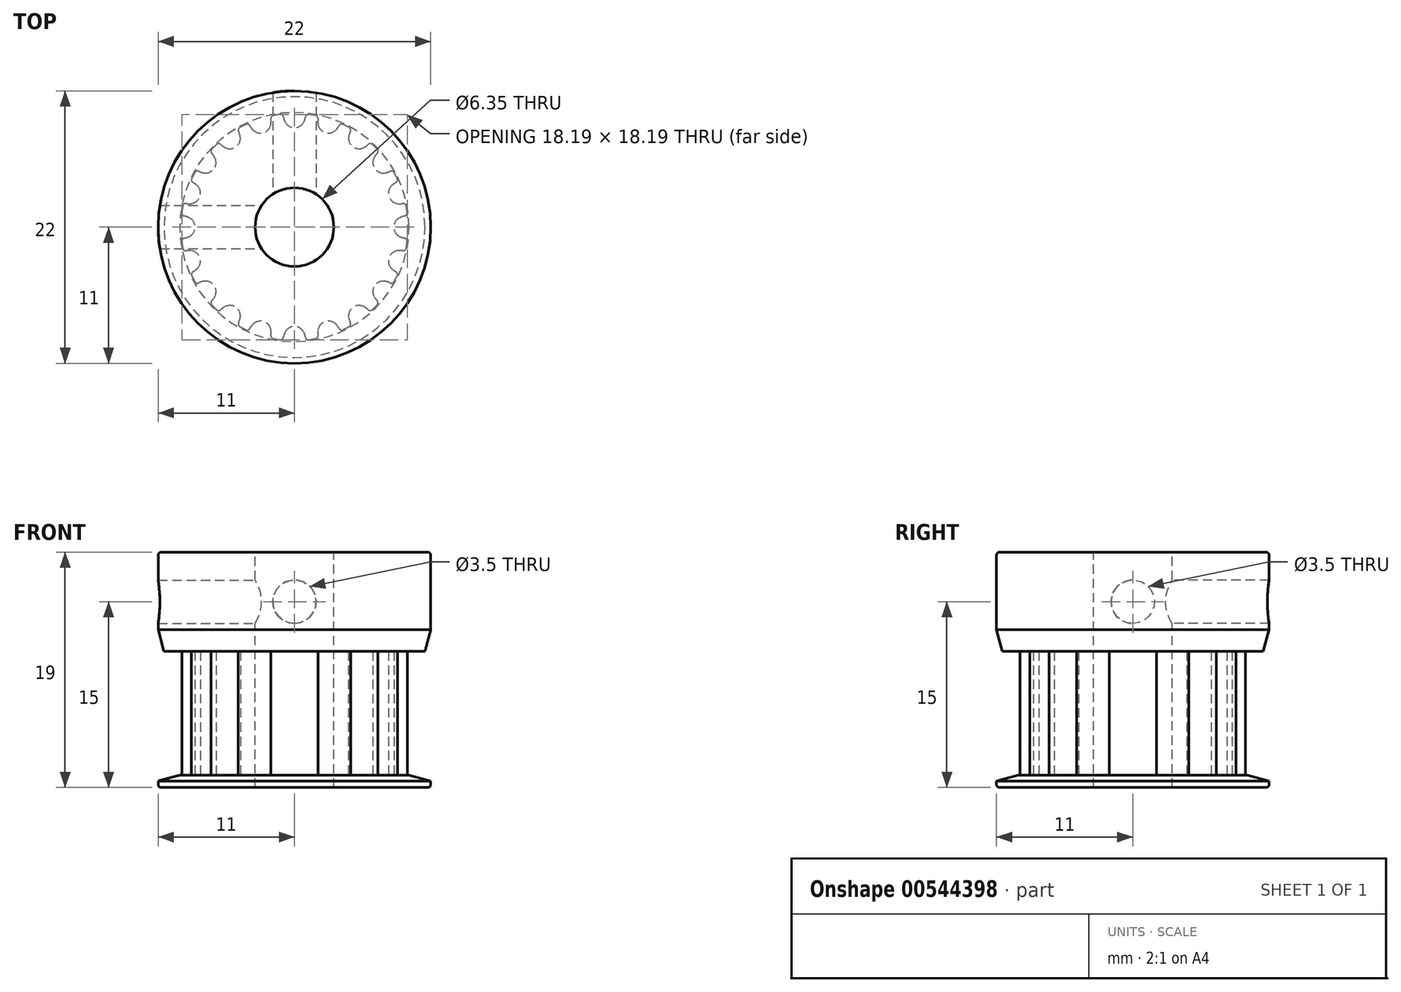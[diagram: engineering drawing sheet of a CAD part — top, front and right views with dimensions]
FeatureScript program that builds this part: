
annotation { "Feature Type Name" : "Feature", "Feature Type Description" : "" }
export const myFeature = defineFeature(function(context is Context, id is Id, definition is map)
    precondition{}
    {
        {
            assignVariable(context, id + "F0", {"name" : "teeth", "anyValue" : 20});
        }
        {
            assignVariable(context, id + "F1", {"name" : "width", "anyValue" : 10});
        }
        {
            var Q0;
            Q0=qCreatedBy(makeId("Top.planeOp"),FACE);
            var sketch = newSketch(context, id + "F2", { "sketchPlane" : qUnion([Q0])});
            skLineSegment(sketch, "E0", {"start": v(0, 0) * mm, "end": v(0, 8.02) * mm, "construction": true});
            skArc(sketch, "E1", {"start": v(2.35, 8.86) * mm, "mid": v(0, 9.17) * mm, "end": v(-2.35, 8.86) * mm, "construction": true});
            skArc(sketch, "E2", {"start": v(0, 8.02) * mm, "mid": v(0.46, 8.15) * mm, "end": v(0.77, 8.52) * mm});
            skLineSegment(sketch, "E3", {"start": v(0, 8.02) * mm, "end": v(0, 9.17) * mm, "construction": true});
            skLineSegment(sketch, "E4", {"start": v(0, 9.17) * mm, "end": v(0, 9.55) * mm, "construction": true});
            skArc(sketch, "E5", {"start": v(1.5, 9.43) * mm, "mid": v(0, 9.55) * mm, "end": v(-1.5, 9.43) * mm, "construction": true});
            skLineSegment(sketch, "E6", {"start": v(1.43, 9.06) * mm, "end": v(0, 0) * mm});
            skLineSegment(sketch, "E7", {"start": v(0, 0) * mm, "end": v(-1.43, 9.06) * mm});
            skArc(sketch, "E8", {"start": v(1.17, 9.1) * mm, "mid": v(0.99, 9.05) * mm, "end": v(0.89, 8.89) * mm});
            skArc(sketch, "E9", {"start": v(0.77, 8.52) * mm, "mid": v(0.84, 8.7) * mm, "end": v(0.89, 8.89) * mm});
            skArc(sketch, "E10.MirrorCS", {"start": v(0, 8.02) * mm, "mid": v(-0.46, 8.15) * mm, "end": v(-0.77, 8.52) * mm});
            skArc(sketch, "E11.MirrorCS", {"start": v(-0.77, 8.52) * mm, "mid": v(-0.84, 8.7) * mm, "end": v(-0.89, 8.89) * mm});
            skArc(sketch, "E12.MirrorCS", {"start": v(-1.17, 9.1) * mm, "mid": v(-0.99, 9.05) * mm, "end": v(-0.89, 8.89) * mm});
            skArc(sketch, "E13", {"start": v(0, 9.17) * mm, "mid": v(-0.3, 9.16) * mm, "end": v(-0.6, 9.15) * mm, "construction": true});
            skArc(sketch, "E14", {"start": v(2.16, 7.72) * mm, "mid": v(0, 8.02) * mm, "end": v(-2.16, 7.72) * mm, "construction": true});
            skArc(sketch, "E15", {"start": v(-1.17, 9.1) * mm, "mid": v(-1.3, 9.08) * mm, "end": v(-1.43, 9.06) * mm});
            skArc(sketch, "E16", {"start": v(1.17, 9.1) * mm, "mid": v(1.3, 9.08) * mm, "end": v(1.43, 9.06) * mm});
            skPoint(sketch, "E17", {"position": v(0, 8.02) * mm});
            skSolve(sketch);
        }
        {
            var Q0;
            Q0=makeQuery(id+"F2.imprint","IMPRINT",FACE,{"disambiguationData":[TD([[makeQuery(id+"F2.imprint","IMPRINT",EDGE,{"derivedFrom":sQuery(id+"F2.wireOp",EDGE,"E2")}),-1.0]])]});
            var Q1;
            {var subQ1=sQuery(id+"F2.wireOp",EDGE,"N9a9pOVT-NxnP-9PMo-Yz0L-ytRW1WlfzG62");Q1=makeQuery(id+"F2.imprint","IMPRINT",FACE,{"disambiguationData":[TD([[makeQuery(id+"F2.imprint","IMPRINT",EDGE,{"derivedFrom":subQ1}),-1.0]])]});}
            var Q2;
            {var subQ0=sQuery(id+"F2.wireOp",EDGE,"E6");Q2=makeQuery(id+"F2.imprint","IMPRINT",FACE,{"disambiguationData":[TD([[makeQuery(id+"F2.imprint","IMPRINT",EDGE,{"derivedFrom":subQ0}),-1.0]])]});}
            extrude(context, id + "F3", {"entities" : qUnion([Q0, Q1, Q2]), "depth" : (getVariable(context, 'width')) * mm, "offsetDistance" : 25 * mm, "symmetric" : true});
        }
        {
            var Q0;
            Q0=makeQuery(id+"F3.opExtrude","SWEPT_BODY",BODY,{"disambiguationData":[OSD([sQuery(id+"F2.wireOp",EDGE,"E1"),sQuery(id+"F2.wireOp",EDGE,"E2"),sQuery(id+"F2.wireOp",EDGE,"WtW3y5By-gfdo-wMA2-XeKf-OYMCoWhlFWBV"),sQuery(id+"F2.wireOp",EDGE,"E6"),sQuery(id+"F2.wireOp",EDGE,"E7"),sQuery(id+"F2.wireOp",EDGE,"N9a9pOVT-NxnP-9PMo-Yz0L-ytRW1WlfzG62"),sQuery(id+"F2.wireOp",EDGE,"E8"),sQuery(id+"F2.wireOp",EDGE,"E9"),sQuery(id+"F2.wireOp",EDGE,"E10.MirrorCS"),sQuery(id+"F2.wireOp",EDGE,"E11.MirrorCS"),sQuery(id+"F2.wireOp",EDGE,"E12.MirrorCS")])]});
            var Q1;
            Q1=makeQuery(id+"F3.opExtrude","SWEPT_EDGE",EDGE,{"disambiguationData":[OSD([sQuery(id+"F2.wireOp",EDGE,"E6"),sQuery(id+"F2.wireOp",EDGE,"E7")])]});
            circularPattern(context, id + "F4", {"operationType" : NewBodyOperationType.ADD, "entities" : qUnion([Q0]), "axis" : qUnion([Q1]), "angle" : 360 * degree, "instanceCount" : getVariable(context, 'teeth'), "equalSpace" : true});
        }
        {
            var Q0;
            {var subQ0=makeQuery(id+"F3.opExtrude","CAP_FACE",FACE,{"disambiguationData":[OSD([sQuery(id+"F2.wireOp",EDGE,"E2"),sQuery(id+"F2.wireOp",EDGE,"E6"),sQuery(id+"F2.wireOp",EDGE,"E7"),sQuery(id+"F2.wireOp",EDGE,"E8"),sQuery(id+"F2.wireOp",EDGE,"E9"),sQuery(id+"F2.wireOp",EDGE,"E10.MirrorCS"),sQuery(id+"F2.wireOp",EDGE,"E11.MirrorCS"),sQuery(id+"F2.wireOp",EDGE,"E12.MirrorCS"),sQuery(id+"F2.wireOp",EDGE,"E15"),sQuery(id+"F2.wireOp",EDGE,"E16")])],"isStart":true});Q0=makeQuery(id+"F4.boolean.opBoolean","MERGE",FACE,{"derivedFrom":[subQ0,makeQuery(id+"F4.opPattern","COPY",FACE,{"derivedFrom":subQ0,"instanceName":"1"}),makeQuery(id+"F4.opPattern","COPY",FACE,{"derivedFrom":subQ0,"instanceName":"2"}),makeQuery(id+"F4.opPattern","COPY",FACE,{"derivedFrom":subQ0,"instanceName":"3"}),makeQuery(id+"F4.opPattern","COPY",FACE,{"derivedFrom":subQ0,"instanceName":"4"}),makeQuery(id+"F4.opPattern","COPY",FACE,{"derivedFrom":subQ0,"instanceName":"5"}),makeQuery(id+"F4.opPattern","COPY",FACE,{"derivedFrom":subQ0,"instanceName":"6"}),makeQuery(id+"F4.opPattern","COPY",FACE,{"derivedFrom":subQ0,"instanceName":"7"}),makeQuery(id+"F4.opPattern","COPY",FACE,{"derivedFrom":subQ0,"instanceName":"8"}),makeQuery(id+"F4.opPattern","COPY",FACE,{"derivedFrom":subQ0,"instanceName":"9"}),makeQuery(id+"F4.opPattern","COPY",FACE,{"derivedFrom":subQ0,"instanceName":"10"}),makeQuery(id+"F4.opPattern","COPY",FACE,{"derivedFrom":subQ0,"instanceName":"11"}),makeQuery(id+"F4.opPattern","COPY",FACE,{"derivedFrom":subQ0,"instanceName":"12"}),makeQuery(id+"F4.opPattern","COPY",FACE,{"derivedFrom":subQ0,"instanceName":"13"}),makeQuery(id+"F4.opPattern","COPY",FACE,{"derivedFrom":subQ0,"instanceName":"14"}),makeQuery(id+"F4.opPattern","COPY",FACE,{"derivedFrom":subQ0,"instanceName":"15"}),makeQuery(id+"F4.opPattern","COPY",FACE,{"derivedFrom":subQ0,"instanceName":"16"}),makeQuery(id+"F4.opPattern","COPY",FACE,{"derivedFrom":subQ0,"instanceName":"17"}),makeQuery(id+"F4.opPattern","COPY",FACE,{"derivedFrom":subQ0,"instanceName":"18"}),makeQuery(id+"F4.opPattern","COPY",FACE,{"derivedFrom":subQ0,"instanceName":"19"}),makeQuery(id+"F4.opPattern","COPY",FACE,{"derivedFrom":subQ0,"instanceName":"20"}),makeQuery(id+"F4.opPattern","COPY",FACE,{"derivedFrom":subQ0,"instanceName":"21"}),makeQuery(id+"F4.opPattern","COPY",FACE,{"derivedFrom":subQ0,"instanceName":"22"}),makeQuery(id+"F4.opPattern","COPY",FACE,{"derivedFrom":subQ0,"instanceName":"23"}),makeQuery(id+"F4.opPattern","COPY",FACE,{"derivedFrom":subQ0,"instanceName":"24"}),makeQuery(id+"F4.opPattern","COPY",FACE,{"derivedFrom":subQ0,"instanceName":"25"}),makeQuery(id+"F4.opPattern","COPY",FACE,{"derivedFrom":subQ0,"instanceName":"26"}),makeQuery(id+"F4.opPattern","COPY",FACE,{"derivedFrom":subQ0,"instanceName":"27"}),makeQuery(id+"F4.opPattern","COPY",FACE,{"derivedFrom":subQ0,"instanceName":"28"}),makeQuery(id+"F4.opPattern","COPY",FACE,{"derivedFrom":subQ0,"instanceName":"29"}),makeQuery(id+"F4.opPattern","COPY",FACE,{"derivedFrom":subQ0,"instanceName":"30"}),makeQuery(id+"F4.opPattern","COPY",FACE,{"derivedFrom":subQ0,"instanceName":"31"}),makeQuery(id+"F4.opPattern","COPY",FACE,{"derivedFrom":subQ0,"instanceName":"32"}),makeQuery(id+"F4.opPattern","COPY",FACE,{"derivedFrom":subQ0,"instanceName":"33"}),makeQuery(id+"F4.opPattern","COPY",FACE,{"derivedFrom":subQ0,"instanceName":"34"}),makeQuery(id+"F4.opPattern","COPY",FACE,{"derivedFrom":subQ0,"instanceName":"35"}),makeQuery(id+"F4.opPattern","COPY",FACE,{"derivedFrom":subQ0,"instanceName":"36"}),makeQuery(id+"F4.opPattern","COPY",FACE,{"derivedFrom":subQ0,"instanceName":"37"}),makeQuery(id+"F4.opPattern","COPY",FACE,{"derivedFrom":subQ0,"instanceName":"38"}),makeQuery(id+"F4.opPattern","COPY",FACE,{"derivedFrom":subQ0,"instanceName":"39"})]});}
            var sketch = newSketch(context, id + "F5", { "sketchPlane" : qUnion([Q0])});
            skCircle(sketch, "E18", {"center": v(0, 0) * mm, "radius": 11 * mm});
            skSolve(sketch);
        }
        {
            var Q0;
            Q0=qSketchRegion(id+"F5",true);
            extrude(context, id + "F6", {"entities" : qUnion([Q0]), "operationType" : NewBodyOperationType.ADD, "depth" : 1 * mm, "offsetDistance" : 25 * mm});
        }
        {
            var Q0;
            {var subQ0=makeQuery(id+"F3.opExtrude","CAP_FACE",FACE,{"disambiguationData":[OSD([sQuery(id+"F2.wireOp",EDGE,"E2"),sQuery(id+"F2.wireOp",EDGE,"E6"),sQuery(id+"F2.wireOp",EDGE,"E7"),sQuery(id+"F2.wireOp",EDGE,"E8"),sQuery(id+"F2.wireOp",EDGE,"E9"),sQuery(id+"F2.wireOp",EDGE,"E10.MirrorCS"),sQuery(id+"F2.wireOp",EDGE,"E11.MirrorCS"),sQuery(id+"F2.wireOp",EDGE,"E12.MirrorCS"),sQuery(id+"F2.wireOp",EDGE,"E15"),sQuery(id+"F2.wireOp",EDGE,"E16")])],"isStart":false});Q0=makeQuery(id+"F4.boolean.opBoolean","MERGE",FACE,{"derivedFrom":[subQ0,makeQuery(id+"F4.opPattern","COPY",FACE,{"derivedFrom":subQ0,"instanceName":"1"}),makeQuery(id+"F4.opPattern","COPY",FACE,{"derivedFrom":subQ0,"instanceName":"2"}),makeQuery(id+"F4.opPattern","COPY",FACE,{"derivedFrom":subQ0,"instanceName":"3"}),makeQuery(id+"F4.opPattern","COPY",FACE,{"derivedFrom":subQ0,"instanceName":"4"}),makeQuery(id+"F4.opPattern","COPY",FACE,{"derivedFrom":subQ0,"instanceName":"5"}),makeQuery(id+"F4.opPattern","COPY",FACE,{"derivedFrom":subQ0,"instanceName":"6"}),makeQuery(id+"F4.opPattern","COPY",FACE,{"derivedFrom":subQ0,"instanceName":"7"}),makeQuery(id+"F4.opPattern","COPY",FACE,{"derivedFrom":subQ0,"instanceName":"8"}),makeQuery(id+"F4.opPattern","COPY",FACE,{"derivedFrom":subQ0,"instanceName":"9"}),makeQuery(id+"F4.opPattern","COPY",FACE,{"derivedFrom":subQ0,"instanceName":"10"}),makeQuery(id+"F4.opPattern","COPY",FACE,{"derivedFrom":subQ0,"instanceName":"11"}),makeQuery(id+"F4.opPattern","COPY",FACE,{"derivedFrom":subQ0,"instanceName":"12"}),makeQuery(id+"F4.opPattern","COPY",FACE,{"derivedFrom":subQ0,"instanceName":"13"}),makeQuery(id+"F4.opPattern","COPY",FACE,{"derivedFrom":subQ0,"instanceName":"14"}),makeQuery(id+"F4.opPattern","COPY",FACE,{"derivedFrom":subQ0,"instanceName":"15"}),makeQuery(id+"F4.opPattern","COPY",FACE,{"derivedFrom":subQ0,"instanceName":"16"}),makeQuery(id+"F4.opPattern","COPY",FACE,{"derivedFrom":subQ0,"instanceName":"17"}),makeQuery(id+"F4.opPattern","COPY",FACE,{"derivedFrom":subQ0,"instanceName":"18"}),makeQuery(id+"F4.opPattern","COPY",FACE,{"derivedFrom":subQ0,"instanceName":"19"}),makeQuery(id+"F4.opPattern","COPY",FACE,{"derivedFrom":subQ0,"instanceName":"20"}),makeQuery(id+"F4.opPattern","COPY",FACE,{"derivedFrom":subQ0,"instanceName":"21"}),makeQuery(id+"F4.opPattern","COPY",FACE,{"derivedFrom":subQ0,"instanceName":"22"}),makeQuery(id+"F4.opPattern","COPY",FACE,{"derivedFrom":subQ0,"instanceName":"23"}),makeQuery(id+"F4.opPattern","COPY",FACE,{"derivedFrom":subQ0,"instanceName":"24"}),makeQuery(id+"F4.opPattern","COPY",FACE,{"derivedFrom":subQ0,"instanceName":"25"}),makeQuery(id+"F4.opPattern","COPY",FACE,{"derivedFrom":subQ0,"instanceName":"26"}),makeQuery(id+"F4.opPattern","COPY",FACE,{"derivedFrom":subQ0,"instanceName":"27"}),makeQuery(id+"F4.opPattern","COPY",FACE,{"derivedFrom":subQ0,"instanceName":"28"}),makeQuery(id+"F4.opPattern","COPY",FACE,{"derivedFrom":subQ0,"instanceName":"29"}),makeQuery(id+"F4.opPattern","COPY",FACE,{"derivedFrom":subQ0,"instanceName":"30"}),makeQuery(id+"F4.opPattern","COPY",FACE,{"derivedFrom":subQ0,"instanceName":"31"}),makeQuery(id+"F4.opPattern","COPY",FACE,{"derivedFrom":subQ0,"instanceName":"32"}),makeQuery(id+"F4.opPattern","COPY",FACE,{"derivedFrom":subQ0,"instanceName":"33"}),makeQuery(id+"F4.opPattern","COPY",FACE,{"derivedFrom":subQ0,"instanceName":"34"}),makeQuery(id+"F4.opPattern","COPY",FACE,{"derivedFrom":subQ0,"instanceName":"35"}),makeQuery(id+"F4.opPattern","COPY",FACE,{"derivedFrom":subQ0,"instanceName":"36"}),makeQuery(id+"F4.opPattern","COPY",FACE,{"derivedFrom":subQ0,"instanceName":"37"}),makeQuery(id+"F4.opPattern","COPY",FACE,{"derivedFrom":subQ0,"instanceName":"38"}),makeQuery(id+"F4.opPattern","COPY",FACE,{"derivedFrom":subQ0,"instanceName":"39"})]});}
            var sketch = newSketch(context, id + "F7", { "sketchPlane" : qUnion([Q0])});
            skCircle(sketch, "E19", {"center": v(0, 0) * mm, "radius": 11 * mm});
            skSolve(sketch);
        }
        {
            var Q0;
            Q0=qSketchRegion(id+"F7",true);
            extrude(context, id + "F8", {"entities" : qUnion([Q0]), "operationType" : NewBodyOperationType.ADD, "depth" : 1 * mm, "offsetDistance" : 25 * mm});
        }
        {
            var Q0;
            Q0=makeQuery(id+"F8.opExtrude","CAP_FACE",FACE,{"disambiguationData":[OSD([sQuery(id+"F7.wireOp",EDGE,"E19")])],"isStart":false});
            var sketch = newSketch(context, id + "F9", { "sketchPlane" : qUnion([Q0])});
            skCircle(sketch, "E20", {"center": v(0, 0) * mm, "radius": 11 * mm});
            skSolve(sketch);
        }
        {
            var Q0;
            Q0=qSketchRegion(id+"F9",true);
            extrude(context, id + "F10", {"entities" : qUnion([Q0]), "operationType" : NewBodyOperationType.ADD, "depth" : 7 * mm, "offsetDistance" : 25 * mm});
        }
        {
            var Q0;
            Q0=makeQuery(id+"F10.opExtrude","CAP_FACE",FACE,{"disambiguationData":[OSD([sQuery(id+"F9.wireOp",EDGE,"E20")])],"isStart":false});
            var sketch = newSketch(context, id + "F11", { "sketchPlane" : qUnion([Q0])});
            skCircle(sketch, "E21", {"center": v(0, 0) * mm, "radius": 3.18 * mm});
            skSolve(sketch);
        }
        {
            var Q0;
            Q0=qSketchRegion(id+"F11",true);
            extrude(context, id + "F12", {"entities" : qUnion([Q0]), "operationType" : NewBodyOperationType.REMOVE, "endBound" : BoundingType.THROUGH_ALL, "oppositeDirection" : true, "depth" : 25 * mm, "offsetDistance" : 25 * mm});
        }
        {
            var Q0;
            Q0=qCreatedBy(makeId("Front.planeOp"),FACE);
            var sketch = newSketch(context, id + "F13", { "sketchPlane" : qUnion([Q0])});
            skCircle(sketch, "E22", {"center": v(0, 9) * mm, "radius": 1.75 * mm});
            skLineSegment(sketch, "E23", {"start": v(18.37, 9) * mm, "end": v(-19.05, 9) * mm, "construction": true});
            skSolve(sketch);
        }
        {
            var Q0;
            Q0=qSketchRegion(id+"F13",true);
            extrude(context, id + "F14", {"entities" : qUnion([Q0]), "operationType" : NewBodyOperationType.REMOVE, "endBound" : BoundingType.THROUGH_ALL, "oppositeDirection" : true, "depth" : 25 * mm, "offsetDistance" : 25 * mm});
        }
        {
            var Q0;
            Q0=qCreatedBy(makeId("Right.planeOp"),FACE);
            var sketch = newSketch(context, id + "F15", { "sketchPlane" : qUnion([Q0])});
            skCircle(sketch, "E24", {"center": v(0, 9) * mm, "radius": 1.75 * mm});
            skLineSegment(sketch, "E25", {"start": v(-13.06, 9) * mm, "end": v(13.09, 9) * mm, "construction": true});
            skSolve(sketch);
        }
        {
            var Q0;
            Q0=qSketchRegion(id+"F15",true);
            extrude(context, id + "F16", {"entities" : qUnion([Q0]), "operationType" : NewBodyOperationType.REMOVE, "endBound" : BoundingType.THROUGH_ALL, "oppositeDirection" : true, "depth" : 25 * mm, "offsetDistance" : 25 * mm});
        }
        {
            var Q0;
            Q0=makeQuery(id+"F6.opExtrude","CAP_EDGE",EDGE,{"disambiguationData":[OSD([sQuery(id+"F5.wireOp",EDGE,"E18")])],"isStart":true});
            var Q1;
            Q1=makeQuery(id+"F8.opExtrude","CAP_EDGE",EDGE,{"disambiguationData":[OSD([sQuery(id+"F7.wireOp",EDGE,"E19")])],"isStart":true});
            chamfer(context, id + "F17", {"entities" : qUnion([Q0, Q1]), "chamferType" : ChamferType.OFFSET_ANGLE, "width" : 1.75 * mm, "oppositeDirection" : true, "angle" : 15 * degree, "tangentPropagation" : true});
        }
        {
            var Q0;
            Q0=makeQuery(id+"F10.opExtrude","CAP_EDGE",EDGE,{"disambiguationData":[OSD([sQuery(id+"F9.wireOp",EDGE,"E20")])],"isStart":true});
            var Q1;
            Q1=makeQuery(id+"F10.opExtrude","CAP_EDGE",EDGE,{"disambiguationData":[OSD([sQuery(id+"F9.wireOp",EDGE,"E20")])],"isStart":false});
            var Q2;
            Q2=makeQuery(id+"F8.opExtrude","CAP_EDGE",EDGE,{"disambiguationData":[OSD([sQuery(id+"F7.wireOp",EDGE,"E19")])],"isStart":false});
            var Q3;
            Q3=makeQuery(id+"F6.opExtrude","CAP_EDGE",EDGE,{"disambiguationData":[OSD([sQuery(id+"F5.wireOp",EDGE,"E18")])],"isStart":false});
            fillet(context, id + "F18", {"entities" : qUnion([Q0, Q1, Q2, Q3]), "radius" : 0.25 * mm, "tangentPropagation" : true, "allowEdgeOverflow" : false});
        }
    });
